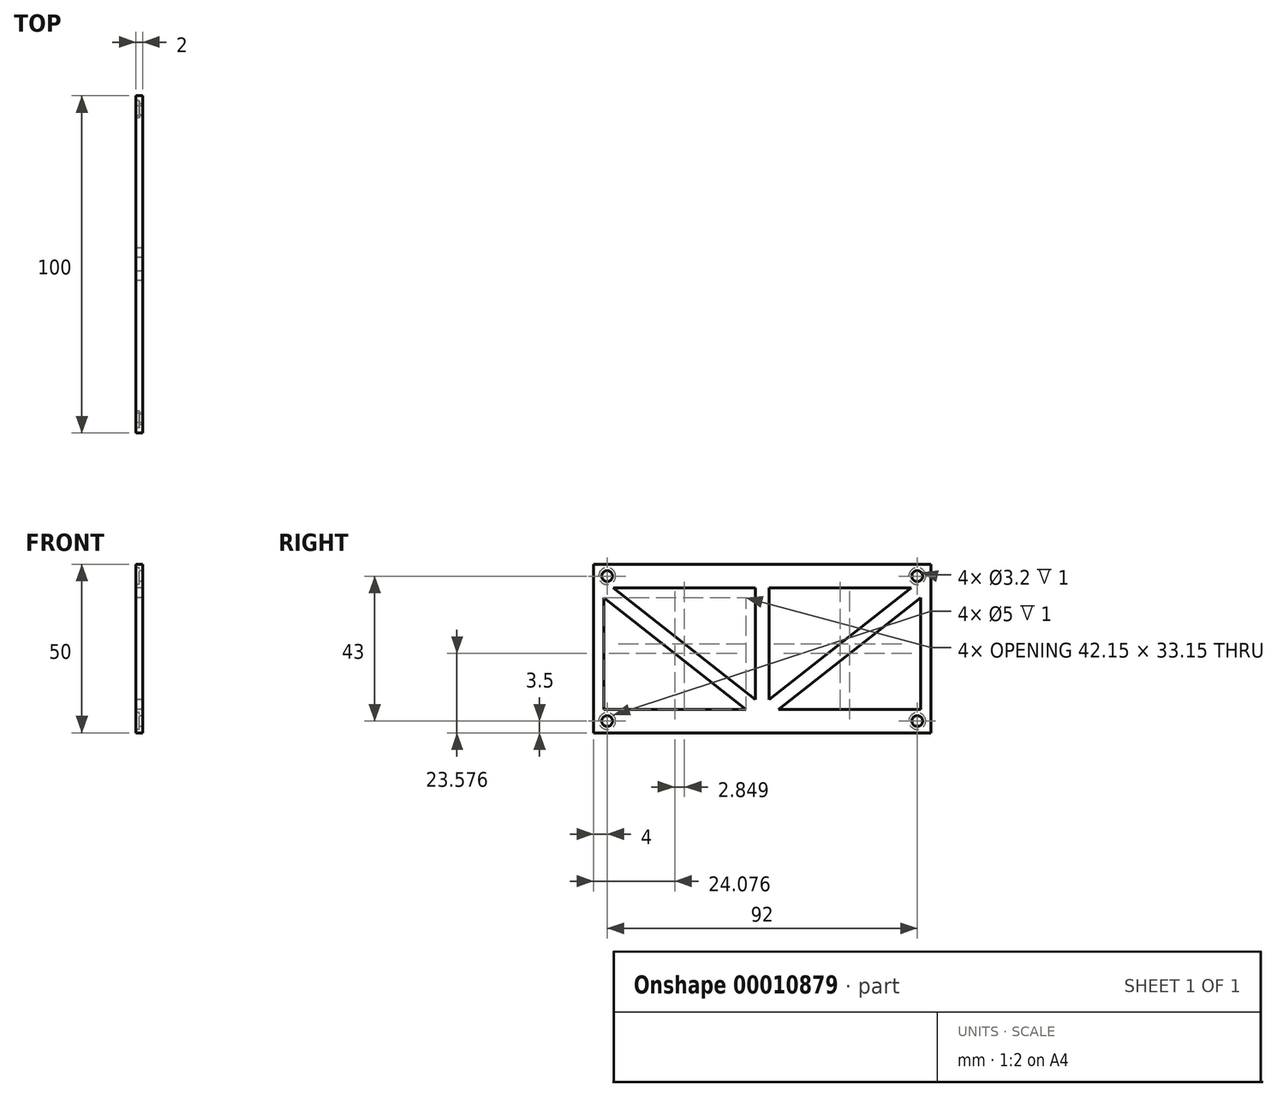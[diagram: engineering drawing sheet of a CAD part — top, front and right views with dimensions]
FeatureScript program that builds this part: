
annotation { "Feature Type Name" : "Feature", "Feature Type Description" : "" }
export const myFeature = defineFeature(function(context is Context, id is Id, definition is map)
    precondition{}
    {
        {
            var Q0;
            Q0=qCreatedBy(makeId("Right.planeOp"),FACE);
            var sketch = newSketch(context, id + "F0", { "sketchPlane" : qUnion([Q0])});
            skLineSegment(sketch, "E0.bottom", {"start": v(-47, 25) * mm, "end": v(-50, 25) * mm});
            skLineSegment(sketch, "E0.top", {"start": v(-47, -25) * mm, "end": v(-50, -25) * mm});
            skLineSegment(sketch, "E0.left", {"start": v(-47, 15.15) * mm, "end": v(-47, -18) * mm});
            skLineSegment(sketch, "E0.right", {"start": v(-50, 25) * mm, "end": v(-50, -25) * mm});
            skLineSegment(sketch, "E1.bottom", {"start": v(-47, 25) * mm, "end": v(47, 25) * mm});
            skLineSegment(sketch, "E2.bottom", {"start": v(-47, -25) * mm, "end": v(47, -25) * mm});
            skLineSegment(sketch, "E3.bottom", {"start": v(47, 25) * mm, "end": v(50, 25) * mm});
            skLineSegment(sketch, "E3.top", {"start": v(47, -25) * mm, "end": v(50, -25) * mm});
            skLineSegment(sketch, "E3.left", {"start": v(47, 15.15) * mm, "end": v(47, -18) * mm});
            skLineSegment(sketch, "E3.right", {"start": v(50, 25) * mm, "end": v(50, -25) * mm});
            skLineSegment(sketch, "E4", {"start": v(-47, -25) * mm, "end": v(-47, -18) * mm, "construction": true});
            skLineSegment(sketch, "E5.left", {"start": v(-2, 18) * mm, "end": v(-2, -15.15) * mm});
            skLineSegment(sketch, "E5.right", {"start": v(2, 18) * mm, "end": v(2, -15.15) * mm});
            skPoint(sketch, "E6", {"position": v(0, 18) * mm});
            skLineSegment(sketch, "E7", {"start": v(-2, 18) * mm, "end": v(2, 18) * mm, "construction": true});
            skLineSegment(sketch, "E8", {"start": v(-2, 18) * mm, "end": v(-44.15, 18) * mm});
            skLineSegment(sketch, "E9", {"start": v(-44.15, 18) * mm, "end": v(-47, 18) * mm, "construction": true});
            skLineSegment(sketch, "E10", {"start": v(-47, 18) * mm, "end": v(-47, 15.15) * mm, "construction": true});
            skLineSegment(sketch, "E11", {"start": v(2, 18) * mm, "end": v(44.15, 18) * mm});
            skLineSegment(sketch, "E12", {"start": v(44.15, 18) * mm, "end": v(47, 18) * mm, "construction": true});
            skLineSegment(sketch, "E13", {"start": v(47, 18) * mm, "end": v(47, 15.15) * mm, "construction": true});
            skLineSegment(sketch, "E14", {"start": v(-4.85, -18) * mm, "end": v(-47, -18) * mm});
            skLineSegment(sketch, "E15", {"start": v(47, -18) * mm, "end": v(4.85, -18) * mm});
            skLineSegment(sketch, "E16", {"start": v(-4.85, -18) * mm, "end": v(-2, -18) * mm, "construction": true});
            skLineSegment(sketch, "E17", {"start": v(-2, -18) * mm, "end": v(-2, -15.15) * mm, "construction": true});
            skLineSegment(sketch, "E18", {"start": v(2, -15.15) * mm, "end": v(2, -18) * mm, "construction": true});
            skLineSegment(sketch, "E19", {"start": v(2, -18) * mm, "end": v(4.85, -18) * mm, "construction": true});
            skLineSegment(sketch, "E20", {"start": v(-47, 15.15) * mm, "end": v(-4.85, -18) * mm});
            skLineSegment(sketch, "E21", {"start": v(-2, -15.15) * mm, "end": v(-44.15, 18) * mm});
            skLineSegment(sketch, "E22", {"start": v(44.15, 18) * mm, "end": v(2, -15.15) * mm});
            skLineSegment(sketch, "E23", {"start": v(4.85, -18) * mm, "end": v(47, 15.15) * mm});
            skLineSegment(sketch, "E24", {"start": v(-23.08, 1.42) * mm, "end": v(-25.55, -1.72) * mm, "construction": true});
            skLineSegment(sketch, "E25", {"start": v(0, 25) * mm, "end": v(0, -25) * mm, "construction": true});
            skLineSegment(sketch, "E26", {"start": v(-47, 18) * mm, "end": v(-47, 25) * mm, "construction": true});
            skPoint(sketch, "E27.visualSharp", {"position": v(-50, 25) * mm});
            skPoint(sketch, "E28.visualSharp", {"position": v(-50, -25) * mm});
            skPoint(sketch, "E29.visualSharp", {"position": v(50, -25) * mm});
            skPoint(sketch, "E30.visualSharp", {"position": v(50, 25) * mm});
            skLineSegment(sketch, "E31", {"start": v(-47, 18) * mm, "end": v(-50, 18) * mm, "construction": true});
            skLineSegment(sketch, "E32", {"start": v(47, 18) * mm, "end": v(50, 18) * mm, "construction": true});
            skCircle(sketch, "E33", {"center": v(-46, 21.5) * mm, "radius": 1.6 * mm});
            skLineSegment(sketch, "E34", {"start": v(-46, 21.5) * mm, "end": v(0, 21.5) * mm, "construction": true});
            skLineSegment(sketch, "E35", {"start": v(0, 21.5) * mm, "end": v(46, 21.5) * mm, "construction": true});
            skCircle(sketch, "E36", {"center": v(46, 21.5) * mm, "radius": 1.6 * mm});
            skLineSegment(sketch, "E37", {"start": v(46, 25) * mm, "end": v(46, 18) * mm, "construction": true});
            skLineSegment(sketch, "E38", {"start": v(-46, -21.5) * mm, "end": v(0, -21.5) * mm, "construction": true});
            skLineSegment(sketch, "E39", {"start": v(0, -21.5) * mm, "end": v(46, -21.5) * mm, "construction": true});
            skCircle(sketch, "E40", {"center": v(-46, -21.5) * mm, "radius": 1.6 * mm});
            skCircle(sketch, "E41", {"center": v(46, -21.5) * mm, "radius": 1.6 * mm});
            skLineSegment(sketch, "E42", {"start": v(46, -18) * mm, "end": v(46, -25) * mm, "construction": true});
            skSolve(sketch);
        }
        {
            var Q0;
            Q0 = qSketchRegion(id + "F0", true);
            extrude(context, id + "F1", {"entities" : qUnion([Q0]), "depth" : 2 * mm});
        }
        {
            var Q0;
            Q0=qCreatedBy(makeId("Right.planeOp"),FACE);
            var sketch = newSketch(context, id + "F2", { "sketchPlane" : qUnion([Q0])});
            skCircle(sketch, "E43", {"center": v(-46, 21.5) * mm, "radius": 2.5 * mm});
            skCircle(sketch, "E44", {"center": v(46, 21.5) * mm, "radius": 2.5 * mm});
            skCircle(sketch, "E45", {"center": v(46, -21.5) * mm, "radius": 2.5 * mm});
            skCircle(sketch, "E46", {"center": v(-46, -21.5) * mm, "radius": 2.5 * mm});
            skSolve(sketch);
        }
        {
            var Q0;
            Q0 = qSketchRegion(id + "F2", true);
            extrude(context, id + "F3", {"entities" : qUnion([Q0]), "operationType" : NewBodyOperationType.REMOVE, "depth" : 1 * mm});
        }
    });
